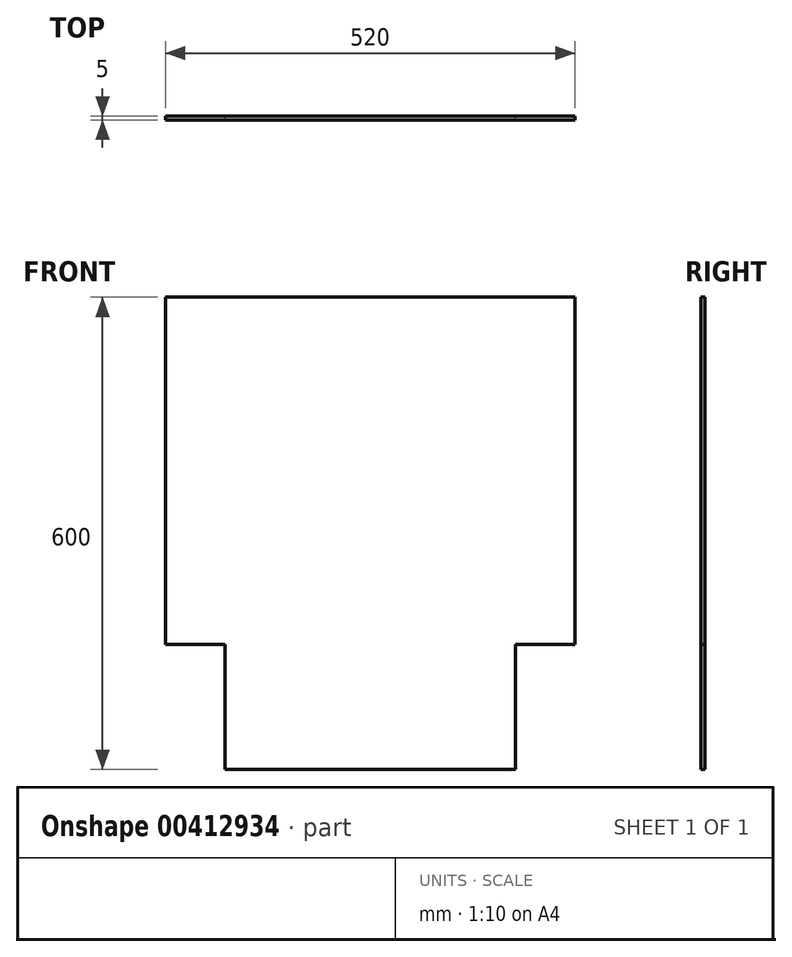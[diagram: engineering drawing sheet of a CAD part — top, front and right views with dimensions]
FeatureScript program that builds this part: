
annotation { "Feature Type Name" : "Feature", "Feature Type Description" : "" }
export const myFeature = defineFeature(function(context is Context, id is Id, definition is map)
    precondition{}
    {
        {
            var Q0;
            Q0=qCreatedBy(makeId("Front.planeOp"),FACE);
            var sketch = newSketch(context, id + "F0", { "sketchPlane" : qUnion([Q0])});
            skLineSegment(sketch, "E0", {"start": v(-260, 0) * mm, "end": v(-260, 277.5) * mm});
            skLineSegment(sketch, "E1", {"start": v(-260, 277.5) * mm, "end": v(0, 277.5) * mm});
            skLineSegment(sketch, "E2", {"start": v(0, 277.5) * mm, "end": v(0, -322.5) * mm});
            skLineSegment(sketch, "E3", {"start": v(0, -322.5) * mm, "end": v(-184.71, -322.5) * mm});
            skLineSegment(sketch, "E4", {"start": v(-184.71, -322.5) * mm, "end": v(-184.71, -163.7) * mm});
            skLineSegment(sketch, "E5", {"start": v(-184.71, -163.7) * mm, "end": v(-260, -163.7) * mm});
            skLineSegment(sketch, "E6", {"start": v(-260, -163.7) * mm, "end": v(-260, 0) * mm});
            skLineSegment(sketch, "E7.MirrorCS", {"start": v(260, 277.5) * mm, "end": v(0, 277.5) * mm});
            skLineSegment(sketch, "E8.MirrorCS", {"start": v(260, 0) * mm, "end": v(260, 277.5) * mm});
            skLineSegment(sketch, "E9.MirrorCS", {"start": v(260, -163.7) * mm, "end": v(260, 0) * mm});
            skLineSegment(sketch, "E10.MirrorCS", {"start": v(184.71, -163.7) * mm, "end": v(260, -163.7) * mm});
            skLineSegment(sketch, "E11.MirrorCS", {"start": v(184.71, -322.5) * mm, "end": v(184.71, -163.7) * mm});
            skLineSegment(sketch, "E12.MirrorCS", {"start": v(0, -322.5) * mm, "end": v(184.71, -322.5) * mm});
            skSolve(sketch);
        }
        {
            var Q0;
            Q0 = qSketchRegion(id + "F0", true);
            extrude(context, id + "F1", {"entities" : qUnion([Q0]), "depth" : 5 * mm});
        }
    });
